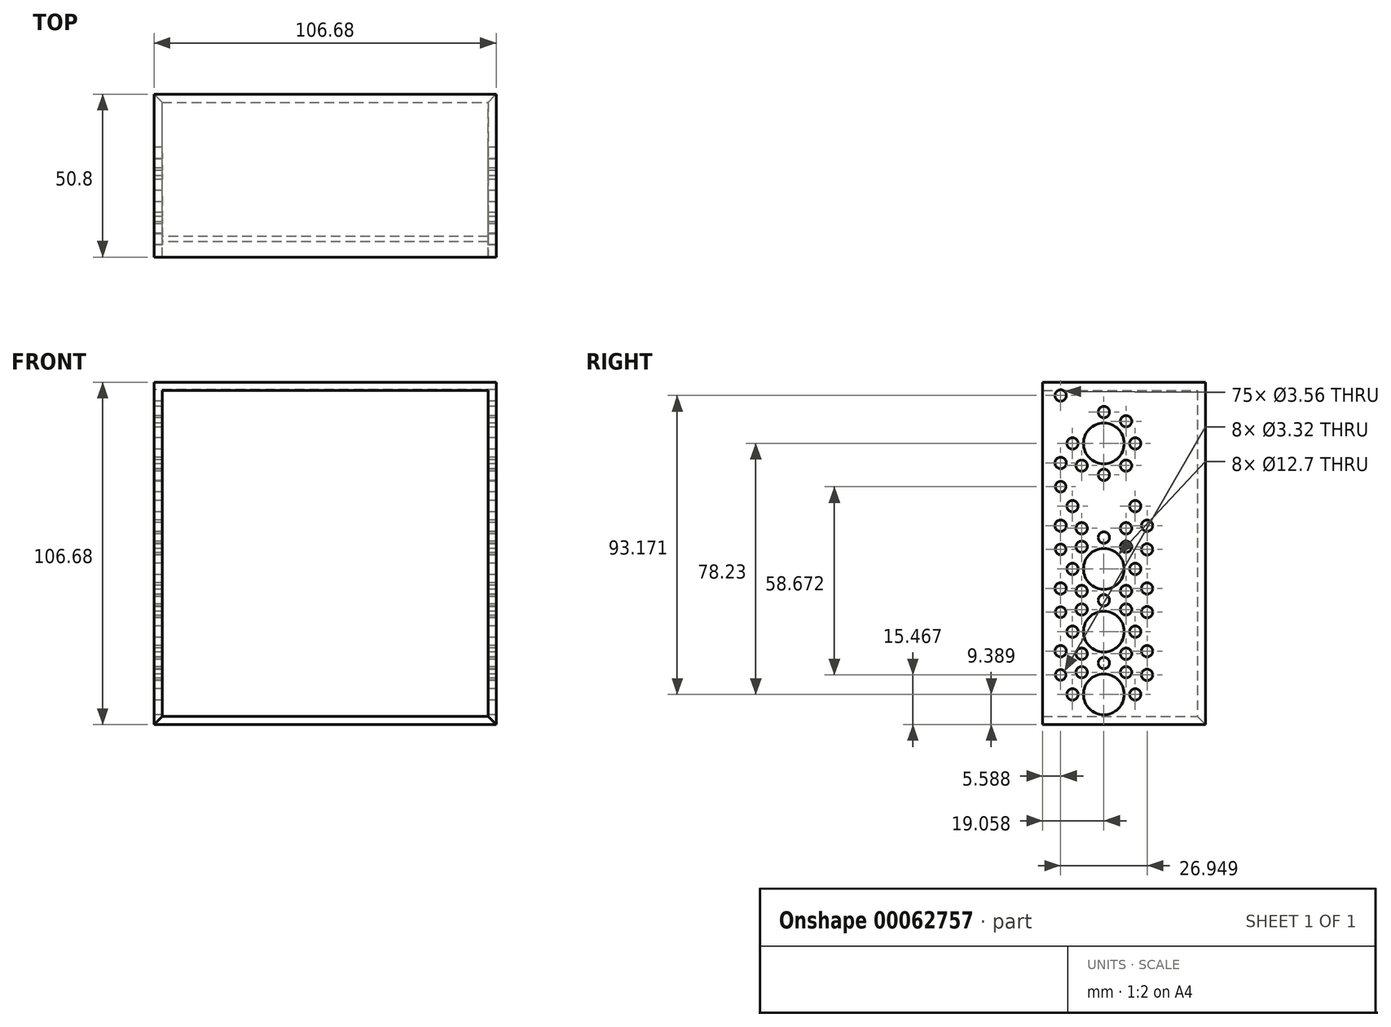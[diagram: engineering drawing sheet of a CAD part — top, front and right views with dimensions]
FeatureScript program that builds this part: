
annotation { "Feature Type Name" : "Feature", "Feature Type Description" : "" }
export const myFeature = defineFeature(function(context is Context, id is Id, definition is map)
    precondition{}
    {
        {
            var Q0;
            Q0=qCreatedBy(makeId("Front.planeOp"),FACE);
            var sketch = newSketch(context, id + "F0", { "sketchPlane" : qUnion([Q0])});
            skLineSegment(sketch, "E0.bottom", {"start": v(-57.75, 57.38) * mm, "end": v(48.93, 57.38) * mm});
            skLineSegment(sketch, "E0.top", {"start": v(-57.75, -49.3) * mm, "end": v(48.93, -49.3) * mm});
            skLineSegment(sketch, "E0.left", {"start": v(-57.75, 57.38) * mm, "end": v(-57.75, -49.3) * mm});
            skLineSegment(sketch, "E0.right", {"start": v(48.93, 57.38) * mm, "end": v(48.93, -49.3) * mm});
            skSolve(sketch);
        }
        {
            var Q0;
            Q0=makeQuery(id+"F0.imprint","IMPRINT",FACE,{"disambiguationData":[TD([[makeQuery(id+"F0.imprint","IMPRINT",EDGE,{"derivedFrom":sQuery(id+"F0.wireOp",EDGE,"E0.bottom")}),-1.0]])]});
            extrude(context, id + "F1", {"entities" : qUnion([Q0]), "depth" : 50.8 * mm});
        }
        {
            var Q0;
            Q0=makeQuery(id+"F1.opExtrude","CAP_FACE",FACE,{"disambiguationData":[OSD([sQuery(id+"F0.wireOp",EDGE,"E0.bottom"),sQuery(id+"F0.wireOp",EDGE,"E0.top"),sQuery(id+"F0.wireOp",EDGE,"E0.left"),sQuery(id+"F0.wireOp",EDGE,"E0.right")])],"isStart":false});
            var Q1;
            Q1=makeQuery(id+"F1.opExtrude","SWEPT_FACE",FACE,{"disambiguationData":[OSD([sQuery(id+"F0.wireOp",EDGE,"E0.top")])]});
            shell(context, id + "F2", {"entities" : qUnion([Q0, Q1]), "thickness" : 2.54 * mm});
        }
        {
            var Q0;
            {var subQ0=sQuery(id+"F0.wireOp",EDGE,"E0.top");Q0=makeQuery(id+"F2.opShell","OFFSET_EDGE",EDGE,{"disambiguationData":[OSD([subQ0]),TDD([makeQuery(id+"F1.opExtrude","CAP_EDGE",EDGE,{"disambiguationData":[OSD([subQ0])],"isStart":true})])]});}
            chamfer(context, id + "F3", {"entities" : qUnion([Q0]), "width" : 2.54 * mm, "tangentPropagation" : true});
        }
        {
            var Q0;
            Q0=makeQuery(id+"F2.opShell","OFFSET_EDGE",EDGE,{"disambiguationData":[OSD([sQuery(id+"F0.wireOp",EDGE,"E0.top"),sQuery(id+"F0.wireOp",EDGE,"E0.left")])]});
            chamfer(context, id + "F4", {"entities" : qUnion([Q0]), "width" : 2.54 * mm, "tangentPropagation" : true});
        }
        {
            var Q0;
            Q0=makeQuery(id+"F2.opShell","OFFSET_EDGE",EDGE,{"disambiguationData":[OSD([sQuery(id+"F0.wireOp",EDGE,"E0.top"),sQuery(id+"F0.wireOp",EDGE,"E0.right")])]});
            chamfer(context, id + "F5", {"entities" : qUnion([Q0]), "width" : 2.54 * mm, "tangentPropagation" : true});
        }
        {
            var Q0;
            Q0=makeQuery(id+"F1.opExtrude","SWEPT_FACE",FACE,{"disambiguationData":[OSD([sQuery(id+"F0.wireOp",EDGE,"E0.left")])]});
            var sketch = newSketch(context, id + "F6", { "sketchPlane" : qUnion([Q0])});
            skCircle(sketch, "E1", {"center": v(45.21, 53.26) * mm, "radius": 1.78 * mm});
            skCircle(sketch, "E2", {"center": v(18.26, 24.84) * mm, "radius": 1.78 * mm});
            skCircle(sketch, "E3", {"center": v(45.21, 24.84) * mm, "radius": 1.66 * mm});
            skCircle(sketch, "E4", {"center": v(38.66, 45.23) * mm, "radius": 1.78 * mm});
            skCircle(sketch, "E5", {"center": v(24.83, 31.4) * mm, "radius": 1.78 * mm});
            skCircle(sketch, "E6", {"center": v(31.74, 38.32) * mm, "radius": 6.35 * mm});
            skCircle(sketch, "E7", {"center": v(38.66, 31.4) * mm, "radius": 1.78 * mm});
            skCircle(sketch, "E8", {"center": v(24.83, 45.23) * mm, "radius": 1.78 * mm});
            skCircle(sketch, "E9", {"center": v(31.74, 48.1) * mm, "radius": 1.78 * mm});
            skCircle(sketch, "E10", {"center": v(21.96, 38.32) * mm, "radius": 1.78 * mm});
            skCircle(sketch, "E11", {"center": v(41.52, 38.32) * mm, "radius": 1.78 * mm});
            skCircle(sketch, "E12", {"center": v(31.74, 28.54) * mm, "radius": 1.78 * mm});
            skCircle(sketch, "E13.0.1.0", {"center": v(31.74, 8.98) * mm, "radius": 1.78 * mm});
            skCircle(sketch, "E13.0.1.1", {"center": v(31.74, 18.76) * mm, "radius": 6.35 * mm});
            skCircle(sketch, "E13.0.1.2", {"center": v(38.66, 11.85) * mm, "radius": 1.78 * mm});
            skCircle(sketch, "E13.0.1.3", {"center": v(41.52, 18.76) * mm, "radius": 1.78 * mm});
            skCircle(sketch, "E13.0.1.4", {"center": v(38.66, 25.68) * mm, "radius": 1.78 * mm});
            skCircle(sketch, "E13.0.1.5", {"center": v(45.21, 32.23) * mm, "radius": 1.78 * mm});
            skCircle(sketch, "E13.0.1.6", {"center": v(45.21, 5.28) * mm, "radius": 1.66 * mm});
            skCircle(sketch, "E13.0.1.7", {"center": v(24.83, 11.85) * mm, "radius": 1.78 * mm});
            skCircle(sketch, "E13.0.1.8", {"center": v(18.26, 5.28) * mm, "radius": 1.78 * mm});
            skCircle(sketch, "E13.0.1.9", {"center": v(21.96, 18.76) * mm, "radius": 1.78 * mm});
            skCircle(sketch, "E13.0.1.10", {"center": v(24.83, 25.68) * mm, "radius": 1.78 * mm});
            skCircle(sketch, "E13.0.1.12", {"center": v(18.26, 32.23) * mm, "radius": 1.78 * mm});
            skCircle(sketch, "E13.0.2.0", {"center": v(31.74, -10.58) * mm, "radius": 1.78 * mm});
            skCircle(sketch, "E13.0.2.1", {"center": v(31.74, -0.8) * mm, "radius": 6.35 * mm});
            skCircle(sketch, "E13.0.2.2", {"center": v(38.66, -7.71) * mm, "radius": 1.78 * mm});
            skCircle(sketch, "E13.0.2.3", {"center": v(41.52, -0.8) * mm, "radius": 1.78 * mm});
            skCircle(sketch, "E13.0.2.4", {"center": v(38.66, 6.12) * mm, "radius": 1.78 * mm});
            skCircle(sketch, "E13.0.2.5", {"center": v(45.21, 12.67) * mm, "radius": 1.78 * mm});
            skCircle(sketch, "E13.0.2.6", {"center": v(45.21, -14.28) * mm, "radius": 1.66 * mm});
            skCircle(sketch, "E13.0.2.7", {"center": v(24.83, -7.71) * mm, "radius": 1.78 * mm});
            skCircle(sketch, "E13.0.2.8", {"center": v(18.26, -14.28) * mm, "radius": 1.78 * mm});
            skCircle(sketch, "E13.0.2.9", {"center": v(21.96, -0.8) * mm, "radius": 1.78 * mm});
            skCircle(sketch, "E13.0.2.10", {"center": v(24.83, 6.12) * mm, "radius": 1.78 * mm});
            skCircle(sketch, "E13.0.2.11", {"center": v(31.74, 8.98) * mm, "radius": 1.78 * mm});
            skCircle(sketch, "E13.0.2.12", {"center": v(18.26, 12.67) * mm, "radius": 1.78 * mm});
            skCircle(sketch, "E13.0.3.0", {"center": v(31.74, -30.13) * mm, "radius": 1.78 * mm});
            skCircle(sketch, "E13.0.3.1", {"center": v(31.74, -20.35) * mm, "radius": 6.35 * mm});
            skCircle(sketch, "E13.0.3.2", {"center": v(38.66, -27.27) * mm, "radius": 1.78 * mm});
            skCircle(sketch, "E13.0.3.3", {"center": v(41.52, -20.35) * mm, "radius": 1.78 * mm});
            skCircle(sketch, "E13.0.3.4", {"center": v(38.66, -13.44) * mm, "radius": 1.78 * mm});
            skCircle(sketch, "E13.0.3.5", {"center": v(45.21, -6.88) * mm, "radius": 1.78 * mm});
            skCircle(sketch, "E13.0.3.6", {"center": v(45.21, -33.83) * mm, "radius": 1.66 * mm});
            skCircle(sketch, "E13.0.3.7", {"center": v(24.83, -27.27) * mm, "radius": 1.78 * mm});
            skCircle(sketch, "E13.0.3.8", {"center": v(18.26, -33.83) * mm, "radius": 1.78 * mm});
            skCircle(sketch, "E13.0.3.9", {"center": v(21.96, -20.35) * mm, "radius": 1.78 * mm});
            skCircle(sketch, "E13.0.3.10", {"center": v(24.83, -13.44) * mm, "radius": 1.78 * mm});
            skCircle(sketch, "E13.0.3.11", {"center": v(31.74, -10.57) * mm, "radius": 1.78 * mm});
            skCircle(sketch, "E13.0.3.12", {"center": v(18.26, -6.88) * mm, "radius": 1.78 * mm});
            skCircle(sketch, "E13.0.4.1", {"center": v(31.74, -39.91) * mm, "radius": 6.35 * mm});
            skCircle(sketch, "E13.0.4.3", {"center": v(41.52, -39.91) * mm, "radius": 1.78 * mm});
            skCircle(sketch, "E13.0.4.4", {"center": v(38.66, -33) * mm, "radius": 1.78 * mm});
            skCircle(sketch, "E13.0.4.5", {"center": v(45.21, -26.44) * mm, "radius": 1.78 * mm});
            skCircle(sketch, "E13.0.4.9", {"center": v(21.96, -39.91) * mm, "radius": 1.78 * mm});
            skCircle(sketch, "E13.0.4.10", {"center": v(24.83, -33) * mm, "radius": 1.78 * mm});
            skCircle(sketch, "E13.0.4.11", {"center": v(31.74, -30.13) * mm, "radius": 1.78 * mm});
            skCircle(sketch, "E13.0.4.12", {"center": v(18.26, -26.44) * mm, "radius": 1.78 * mm});
            skLineSegment(sketch, "E13.direction2", {"start": v(31.74, 28.54) * mm, "end": v(31.74, 8.98) * mm, "construction": true});
            skCircle(sketch, "E14", {"center": v(24.83, 49.96) * mm, "radius": 1.78 * mm});
            skCircle(sketch, "E15", {"center": v(38.66, 49.96) * mm, "radius": 1.78 * mm});
            skCircle(sketch, "E16", {"center": v(45.21, 45.36) * mm, "radius": 1.78 * mm});
            skCircle(sketch, "E17", {"center": v(18.26, 53.31) * mm, "radius": 1.78 * mm});
            skCircle(sketch, "E18", {"center": v(18.26, 45.25) * mm, "radius": 1.78 * mm});
            skSolve(sketch);
        }
        {
            var Q0;
            Q0=makeQuery(id+"F6.imprint","IMPRINT",FACE,{"disambiguationData":[TD([[makeQuery(id+"F6.imprint","IMPRINT",EDGE,{"derivedFrom":sQuery(id+"F6.wireOp",EDGE,"E3")}),1.0]])]});
            var Q1;
            Q1=makeQuery(id+"F6.imprint","IMPRINT",FACE,{"disambiguationData":[TD([[makeQuery(id+"F6.imprint","IMPRINT",EDGE,{"derivedFrom":sQuery(id+"F6.wireOp",EDGE,"E5")}),1.0]])]});
            var Q2;
            Q2=makeQuery(id+"F6.imprint","IMPRINT",FACE,{"disambiguationData":[TD([[makeQuery(id+"F6.imprint","IMPRINT",EDGE,{"derivedFrom":sQuery(id+"F6.wireOp",EDGE,"E7")}),1.0]])]});
            var Q3;
            Q3=makeQuery(id+"F6.imprint","IMPRINT",FACE,{"disambiguationData":[TD([[makeQuery(id+"F6.imprint","IMPRINT",EDGE,{"derivedFrom":sQuery(id+"F6.wireOp",EDGE,"E8")}),1.0]])]});
            var Q4;
            Q4=makeQuery(id+"F6.imprint","IMPRINT",FACE,{"disambiguationData":[TD([[makeQuery(id+"F6.imprint","IMPRINT",EDGE,{"derivedFrom":sQuery(id+"F6.wireOp",EDGE,"E9")}),1.0]])]});
            var Q5;
            Q5=makeQuery(id+"F6.imprint","IMPRINT",FACE,{"disambiguationData":[TD([[makeQuery(id+"F6.imprint","IMPRINT",EDGE,{"derivedFrom":sQuery(id+"F6.wireOp",EDGE,"E10")}),1.0]])]});
            var Q6;
            Q6=makeQuery(id+"F6.imprint","IMPRINT",FACE,{"disambiguationData":[TD([[makeQuery(id+"F6.imprint","IMPRINT",EDGE,{"derivedFrom":sQuery(id+"F6.wireOp",EDGE,"E11")}),1.0]])]});
            var Q7;
            Q7=makeQuery(id+"F6.imprint","IMPRINT",FACE,{"disambiguationData":[TD([[makeQuery(id+"F6.imprint","IMPRINT",EDGE,{"derivedFrom":sQuery(id+"F6.wireOp",EDGE,"E13.0.1.2")}),1.0]])]});
            var Q8;
            Q8=makeQuery(id+"F6.imprint","IMPRINT",FACE,{"disambiguationData":[TD([[makeQuery(id+"F6.imprint","IMPRINT",EDGE,{"derivedFrom":sQuery(id+"F6.wireOp",EDGE,"E13.0.1.3")}),1.0]])]});
            var Q9;
            Q9=makeQuery(id+"F6.imprint","IMPRINT",FACE,{"disambiguationData":[TD([[makeQuery(id+"F6.imprint","IMPRINT",EDGE,{"derivedFrom":sQuery(id+"F6.wireOp",EDGE,"E13.0.1.5")}),1.0]])]});
            var Q10;
            Q10=makeQuery(id+"F6.imprint","IMPRINT",FACE,{"disambiguationData":[TD([[makeQuery(id+"F6.imprint","IMPRINT",EDGE,{"derivedFrom":sQuery(id+"F6.wireOp",EDGE,"E13.0.1.6")}),1.0]])]});
            var Q11;
            Q11=makeQuery(id+"F6.imprint","IMPRINT",FACE,{"disambiguationData":[TD([[makeQuery(id+"F6.imprint","IMPRINT",EDGE,{"derivedFrom":sQuery(id+"F6.wireOp",EDGE,"E13.0.1.7")}),1.0]])]});
            var Q12;
            Q12=makeQuery(id+"F6.imprint","IMPRINT",FACE,{"disambiguationData":[TD([[makeQuery(id+"F6.imprint","IMPRINT",EDGE,{"derivedFrom":sQuery(id+"F6.wireOp",EDGE,"E13.0.1.8")}),1.0]])]});
            var Q13;
            Q13=makeQuery(id+"F6.imprint","IMPRINT",FACE,{"disambiguationData":[TD([[makeQuery(id+"F6.imprint","IMPRINT",EDGE,{"derivedFrom":sQuery(id+"F6.wireOp",EDGE,"E13.0.1.9")}),1.0]])]});
            var Q14;
            Q14=makeQuery(id+"F6.imprint","IMPRINT",FACE,{"disambiguationData":[TD([[makeQuery(id+"F6.imprint","IMPRINT",EDGE,{"derivedFrom":sQuery(id+"F6.wireOp",EDGE,"E13.0.2.1")}),1.0]])]});
            var Q15;
            Q15=makeQuery(id+"F6.imprint","IMPRINT",FACE,{"disambiguationData":[TD([[makeQuery(id+"F6.imprint","IMPRINT",EDGE,{"derivedFrom":sQuery(id+"F6.wireOp",EDGE,"E13.0.2.2")}),1.0]])]});
            var Q16;
            Q16=makeQuery(id+"F6.imprint","IMPRINT",FACE,{"disambiguationData":[TD([[makeQuery(id+"F6.imprint","IMPRINT",EDGE,{"derivedFrom":sQuery(id+"F6.wireOp",EDGE,"E13.0.2.3")}),1.0]])]});
            var Q17;
            Q17=makeQuery(id+"F6.imprint","IMPRINT",FACE,{"disambiguationData":[TD([[makeQuery(id+"F6.imprint","IMPRINT",EDGE,{"derivedFrom":sQuery(id+"F6.wireOp",EDGE,"E13.0.2.4")}),1.0]])]});
            var Q18;
            Q18=makeQuery(id+"F6.imprint","IMPRINT",FACE,{"disambiguationData":[TD([[makeQuery(id+"F6.imprint","IMPRINT",EDGE,{"derivedFrom":sQuery(id+"F6.wireOp",EDGE,"E13.0.2.5")}),1.0]])]});
            var Q19;
            Q19=makeQuery(id+"F6.imprint","IMPRINT",FACE,{"disambiguationData":[TD([[makeQuery(id+"F6.imprint","IMPRINT",EDGE,{"derivedFrom":sQuery(id+"F6.wireOp",EDGE,"E13.0.2.6")}),1.0]])]});
            var Q20;
            Q20=makeQuery(id+"F6.imprint","IMPRINT",FACE,{"disambiguationData":[TD([[makeQuery(id+"F6.imprint","IMPRINT",EDGE,{"derivedFrom":sQuery(id+"F6.wireOp",EDGE,"E13.0.2.7")}),1.0]])]});
            var Q21;
            Q21=makeQuery(id+"F6.imprint","IMPRINT",FACE,{"disambiguationData":[TD([[makeQuery(id+"F6.imprint","IMPRINT",EDGE,{"derivedFrom":sQuery(id+"F6.wireOp",EDGE,"E13.0.2.8")}),1.0]])]});
            var Q22;
            Q22=makeQuery(id+"F6.imprint","IMPRINT",FACE,{"disambiguationData":[TD([[makeQuery(id+"F6.imprint","IMPRINT",EDGE,{"derivedFrom":sQuery(id+"F6.wireOp",EDGE,"E13.0.2.9")}),1.0]])]});
            var Q23;
            Q23=makeQuery(id+"F6.imprint","IMPRINT",FACE,{"disambiguationData":[TD([[makeQuery(id+"F6.imprint","IMPRINT",EDGE,{"derivedFrom":sQuery(id+"F6.wireOp",EDGE,"E13.0.2.10")}),1.0]])]});
            var Q24;
            Q24=makeQuery(id+"F6.imprint","IMPRINT",FACE,{"disambiguationData":[TD([[makeQuery(id+"F6.imprint","IMPRINT",EDGE,{"derivedFrom":sQuery(id+"F6.wireOp",EDGE,"E13.0.2.12")}),1.0]])]});
            var Q25;
            Q25=makeQuery(id+"F6.imprint","IMPRINT",FACE,{"disambiguationData":[TD([[makeQuery(id+"F6.imprint","IMPRINT",EDGE,{"derivedFrom":sQuery(id+"F6.wireOp",EDGE,"E13.0.3.1")}),1.0]])]});
            var Q26;
            Q26=makeQuery(id+"F6.imprint","IMPRINT",FACE,{"disambiguationData":[TD([[makeQuery(id+"F6.imprint","IMPRINT",EDGE,{"derivedFrom":sQuery(id+"F6.wireOp",EDGE,"E13.0.3.2")}),1.0]])]});
            var Q27;
            Q27=makeQuery(id+"F6.imprint","IMPRINT",FACE,{"disambiguationData":[TD([[makeQuery(id+"F6.imprint","IMPRINT",EDGE,{"derivedFrom":sQuery(id+"F6.wireOp",EDGE,"E13.0.3.3")}),1.0]])]});
            var Q28;
            Q28=makeQuery(id+"F6.imprint","IMPRINT",FACE,{"disambiguationData":[TD([[makeQuery(id+"F6.imprint","IMPRINT",EDGE,{"derivedFrom":sQuery(id+"F6.wireOp",EDGE,"E13.0.3.4")}),1.0]])]});
            var Q29;
            Q29=makeQuery(id+"F6.imprint","IMPRINT",FACE,{"disambiguationData":[TD([[makeQuery(id+"F6.imprint","IMPRINT",EDGE,{"derivedFrom":sQuery(id+"F6.wireOp",EDGE,"E13.0.3.5")}),1.0]])]});
            var Q30;
            Q30=makeQuery(id+"F6.imprint","IMPRINT",FACE,{"disambiguationData":[TD([[makeQuery(id+"F6.imprint","IMPRINT",EDGE,{"derivedFrom":sQuery(id+"F6.wireOp",EDGE,"E13.0.3.6")}),1.0]])]});
            var Q31;
            Q31=makeQuery(id+"F6.imprint","IMPRINT",FACE,{"disambiguationData":[TD([[makeQuery(id+"F6.imprint","IMPRINT",EDGE,{"derivedFrom":sQuery(id+"F6.wireOp",EDGE,"E13.0.3.7")}),1.0]])]});
            var Q32;
            Q32=makeQuery(id+"F6.imprint","IMPRINT",FACE,{"disambiguationData":[TD([[makeQuery(id+"F6.imprint","IMPRINT",EDGE,{"derivedFrom":sQuery(id+"F6.wireOp",EDGE,"E13.0.3.8")}),1.0]])]});
            var Q33;
            Q33=makeQuery(id+"F6.imprint","IMPRINT",FACE,{"disambiguationData":[TD([[makeQuery(id+"F6.imprint","IMPRINT",EDGE,{"derivedFrom":sQuery(id+"F6.wireOp",EDGE,"E13.0.3.9")}),1.0]])]});
            var Q34;
            Q34=makeQuery(id+"F6.imprint","IMPRINT",FACE,{"disambiguationData":[TD([[makeQuery(id+"F6.imprint","IMPRINT",EDGE,{"derivedFrom":sQuery(id+"F6.wireOp",EDGE,"E13.0.3.10")}),1.0]])]});
            var Q35;
            Q35=makeQuery(id+"F6.imprint","IMPRINT",FACE,{"disambiguationData":[TD([[makeQuery(id+"F6.imprint","IMPRINT",EDGE,{"derivedFrom":sQuery(id+"F6.wireOp",EDGE,"E13.0.3.12")}),1.0]])]});
            var Q36;
            Q36=makeQuery(id+"F6.imprint","IMPRINT",FACE,{"disambiguationData":[TD([[makeQuery(id+"F6.imprint","IMPRINT",EDGE,{"derivedFrom":sQuery(id+"F6.wireOp",EDGE,"E13.0.4.1")}),1.0]])]});
            var Q37;
            Q37=makeQuery(id+"F6.imprint","IMPRINT",FACE,{"disambiguationData":[TD([[makeQuery(id+"F6.imprint","IMPRINT",EDGE,{"derivedFrom":sQuery(id+"F6.wireOp",EDGE,"E13.0.4.3")}),1.0]])]});
            var Q38;
            Q38=makeQuery(id+"F6.imprint","IMPRINT",FACE,{"disambiguationData":[TD([[makeQuery(id+"F6.imprint","IMPRINT",EDGE,{"derivedFrom":sQuery(id+"F6.wireOp",EDGE,"E13.0.4.4")}),1.0]])]});
            var Q39;
            Q39=makeQuery(id+"F6.imprint","IMPRINT",FACE,{"disambiguationData":[TD([[makeQuery(id+"F6.imprint","IMPRINT",EDGE,{"derivedFrom":sQuery(id+"F6.wireOp",EDGE,"E13.0.4.5")}),1.0]])]});
            var Q40;
            Q40=makeQuery(id+"F6.imprint","IMPRINT",FACE,{"disambiguationData":[TD([[makeQuery(id+"F6.imprint","IMPRINT",EDGE,{"derivedFrom":sQuery(id+"F6.wireOp",EDGE,"E13.0.4.9")}),1.0]])]});
            var Q41;
            Q41=makeQuery(id+"F6.imprint","IMPRINT",FACE,{"disambiguationData":[TD([[makeQuery(id+"F6.imprint","IMPRINT",EDGE,{"derivedFrom":sQuery(id+"F6.wireOp",EDGE,"E13.0.4.10")}),1.0]])]});
            var Q42;
            Q42=makeQuery(id+"F6.imprint","IMPRINT",FACE,{"disambiguationData":[TD([[makeQuery(id+"F6.imprint","IMPRINT",EDGE,{"derivedFrom":sQuery(id+"F6.wireOp",EDGE,"E13.0.4.12")}),1.0]])]});
            var Q43;
            {var subQ0=sQuery(id+"F6.wireOp",EDGE,"A2h9f5pg-UWyG-NB71-LqB8-NmD9h6sl18N1");var subQ1=sQuery(id+"F6.wireOp",EDGE,"vdxriytp-X9rP-He6E-1Lm6-v2A8iyULkwqD");var subQ2=makeQuery(id+"F6.imprint","INTERSECT",VERTEX,{"derivedFrom":[subQ1,subQ0]});Q43=makeQuery(id+"F6.imprint","IMPRINT",FACE,{"disambiguationData":[TD([[makeQuery(id+"F6.imprint","IMPRINT",EDGE,{"disambiguationData":[TD([[subQ2,1.0]])],"derivedFrom":subQ1}),-1.0]])]});}
            var Q44;
            {var subQ0=sQuery(id+"F6.wireOp",EDGE,"A2h9f5pg-UWyG-NB71-LqB8-NmD9h6sl18N1");var subQ1=sQuery(id+"F6.wireOp",EDGE,"vdxriytp-X9rP-He6E-1Lm6-v2A8iyULkwqD");var subQ2=makeQuery(id+"F6.imprint","INTERSECT",VERTEX,{"derivedFrom":[subQ1,subQ0]});Q44=makeQuery(id+"F6.imprint","IMPRINT",FACE,{"disambiguationData":[TD([[makeQuery(id+"F6.imprint","IMPRINT",EDGE,{"disambiguationData":[TD([[subQ2,1.0]])],"derivedFrom":subQ1}),1.0]])]});}
            var Q45;
            {var subQ0=sQuery(id+"F6.wireOp",EDGE,"E13.0.1.12");var subQ1=sQuery(id+"F6.wireOp",EDGE,"A2h9f5pg-UWyG-NB71-LqB8-NmD9h6sl18N1");var subQ2=makeQuery(id+"F6.imprint","INTERSECT",VERTEX,{"disambiguationData":[OD(0.0)],"derivedFrom":[subQ1,subQ0]});Q45=makeQuery(id+"F6.imprint","IMPRINT",FACE,{"disambiguationData":[TD([[makeQuery(id+"F6.imprint","IMPRINT",EDGE,{"disambiguationData":[TD([[subQ2,1.0]])],"derivedFrom":subQ1}),-1.0]])]});}
            var Q46;
            {var subQ0=sQuery(id+"F6.wireOp",EDGE,"E13.0.1.12");var subQ1=sQuery(id+"F6.wireOp",EDGE,"A2h9f5pg-UWyG-NB71-LqB8-NmD9h6sl18N1");var subQ2=makeQuery(id+"F6.imprint","INTERSECT",VERTEX,{"disambiguationData":[OD(0.0)],"derivedFrom":[subQ1,subQ0]});Q46=makeQuery(id+"F6.imprint","IMPRINT",FACE,{"disambiguationData":[TD([[makeQuery(id+"F6.imprint","IMPRINT",EDGE,{"disambiguationData":[TD([[subQ2,1.0]])],"derivedFrom":subQ1}),1.0]])]});}
            var Q47;
            {var subQ0=sQuery(id+"F6.wireOp",EDGE,"owMZy3Z5-PBnJ-gcCq-pzpr-cYzJ99XcFTPD");var subQ1=sQuery(id+"F6.wireOp",EDGE,"A2h9f5pg-UWyG-NB71-LqB8-NmD9h6sl18N1");var subQ2=makeQuery(id+"F6.imprint","INTERSECT",VERTEX,{"derivedFrom":[subQ1,subQ0]});Q47=makeQuery(id+"F6.imprint","IMPRINT",FACE,{"disambiguationData":[TD([[makeQuery(id+"F6.imprint","IMPRINT",EDGE,{"disambiguationData":[TD([[subQ2,1.0]])],"derivedFrom":subQ1}),1.0]])]});}
            var Q48;
            {var subQ0=sQuery(id+"F6.wireOp",EDGE,"owMZy3Z5-PBnJ-gcCq-pzpr-cYzJ99XcFTPD");var subQ1=sQuery(id+"F6.wireOp",EDGE,"A2h9f5pg-UWyG-NB71-LqB8-NmD9h6sl18N1");var subQ2=makeQuery(id+"F6.imprint","INTERSECT",VERTEX,{"derivedFrom":[subQ1,subQ0]});Q48=makeQuery(id+"F6.imprint","IMPRINT",FACE,{"disambiguationData":[TD([[makeQuery(id+"F6.imprint","IMPRINT",EDGE,{"disambiguationData":[TD([[subQ2,1.0]])],"derivedFrom":subQ1}),-1.0]])]});}
            var Q49;
            {var subQ0=sQuery(id+"F6.wireOp",EDGE,"E13.0.1.10");var subQ1=sQuery(id+"F6.wireOp",EDGE,"owMZy3Z5-PBnJ-gcCq-pzpr-cYzJ99XcFTPD");var subQ2=makeQuery(id+"F6.imprint","INTERSECT",VERTEX,{"disambiguationData":[OD(0.0)],"derivedFrom":[subQ1,subQ0]});Q49=makeQuery(id+"F6.imprint","IMPRINT",FACE,{"disambiguationData":[TD([[makeQuery(id+"F6.imprint","IMPRINT",EDGE,{"disambiguationData":[TD([[subQ2,1.0]])],"derivedFrom":subQ1}),-1.0]])]});}
            var Q50;
            {var subQ0=sQuery(id+"F6.wireOp",EDGE,"E13.0.1.10");var subQ1=sQuery(id+"F6.wireOp",EDGE,"owMZy3Z5-PBnJ-gcCq-pzpr-cYzJ99XcFTPD");var subQ2=makeQuery(id+"F6.imprint","INTERSECT",VERTEX,{"disambiguationData":[OD(0.0)],"derivedFrom":[subQ1,subQ0]});Q50=makeQuery(id+"F6.imprint","IMPRINT",FACE,{"disambiguationData":[TD([[makeQuery(id+"F6.imprint","IMPRINT",EDGE,{"disambiguationData":[TD([[subQ2,1.0]])],"derivedFrom":subQ1}),1.0]])]});}
            var Q51;
            {var subQ0=sQuery(id+"F6.wireOp",EDGE,"E13.0.1.1");var subQ1=sQuery(id+"F6.wireOp",EDGE,"owMZy3Z5-PBnJ-gcCq-pzpr-cYzJ99XcFTPD");var subQ2=makeQuery(id+"F6.imprint","INTERSECT",VERTEX,{"disambiguationData":[OD(0.0)],"derivedFrom":[subQ1,subQ0]});Q51=makeQuery(id+"F6.imprint","IMPRINT",FACE,{"disambiguationData":[TD([[makeQuery(id+"F6.imprint","IMPRINT",EDGE,{"disambiguationData":[TD([[subQ2,1.0]])],"derivedFrom":subQ1}),1.0]])]});}
            var Q52;
            {var subQ0=sQuery(id+"F6.wireOp",EDGE,"E13.0.1.1");var subQ1=sQuery(id+"F6.wireOp",EDGE,"owMZy3Z5-PBnJ-gcCq-pzpr-cYzJ99XcFTPD");var subQ2=makeQuery(id+"F6.imprint","INTERSECT",VERTEX,{"disambiguationData":[OD(0.0)],"derivedFrom":[subQ1,subQ0]});Q52=makeQuery(id+"F6.imprint","IMPRINT",FACE,{"disambiguationData":[TD([[makeQuery(id+"F6.imprint","IMPRINT",EDGE,{"disambiguationData":[TD([[subQ2,1.0]])],"derivedFrom":subQ1}),-1.0]])]});}
            var Q53;
            {var subQ0=sQuery(id+"F6.wireOp",EDGE,"E13.0.1.4");var subQ1=sQuery(id+"F6.wireOp",EDGE,"owMZy3Z5-PBnJ-gcCq-pzpr-cYzJ99XcFTPD");var subQ2=makeQuery(id+"F6.imprint","INTERSECT",VERTEX,{"disambiguationData":[OD(0.0)],"derivedFrom":[subQ1,subQ0]});Q53=makeQuery(id+"F6.imprint","IMPRINT",FACE,{"disambiguationData":[TD([[makeQuery(id+"F6.imprint","IMPRINT",EDGE,{"disambiguationData":[TD([[subQ2,1.0]])],"derivedFrom":subQ1}),-1.0]])]});}
            var Q54;
            {var subQ0=sQuery(id+"F6.wireOp",EDGE,"E13.0.1.4");var subQ1=sQuery(id+"F6.wireOp",EDGE,"owMZy3Z5-PBnJ-gcCq-pzpr-cYzJ99XcFTPD");var subQ2=makeQuery(id+"F6.imprint","INTERSECT",VERTEX,{"disambiguationData":[OD(0.0)],"derivedFrom":[subQ1,subQ0]});Q54=makeQuery(id+"F6.imprint","IMPRINT",FACE,{"disambiguationData":[TD([[makeQuery(id+"F6.imprint","IMPRINT",EDGE,{"disambiguationData":[TD([[subQ2,1.0]])],"derivedFrom":subQ1}),1.0]])]});}
            var Q55;
            {var subQ0=sQuery(id+"F6.wireOp",EDGE,"KO0H5Guw-bcFE-xj2E-t414-NG06jMZt0GET");var subQ1=sQuery(id+"F6.wireOp",EDGE,"slbY2Bo9-q9ib-zJOt-UMSs-wo7bCMDzegcF");var subQ2=makeQuery(id+"F6.imprint","INTERSECT",VERTEX,{"derivedFrom":[subQ1,subQ0]});Q55=makeQuery(id+"F6.imprint","IMPRINT",FACE,{"disambiguationData":[TD([[makeQuery(id+"F6.imprint","IMPRINT",EDGE,{"disambiguationData":[TD([[subQ2,1.0]])],"derivedFrom":subQ1}),-1.0]])]});}
            var Q56;
            {var subQ0=sQuery(id+"F6.wireOp",EDGE,"KO0H5Guw-bcFE-xj2E-t414-NG06jMZt0GET");var subQ1=sQuery(id+"F6.wireOp",EDGE,"slbY2Bo9-q9ib-zJOt-UMSs-wo7bCMDzegcF");var subQ2=makeQuery(id+"F6.imprint","INTERSECT",VERTEX,{"derivedFrom":[subQ1,subQ0]});Q56=makeQuery(id+"F6.imprint","IMPRINT",FACE,{"disambiguationData":[TD([[makeQuery(id+"F6.imprint","IMPRINT",EDGE,{"disambiguationData":[TD([[subQ2,1.0]])],"derivedFrom":subQ1}),1.0]])]});}
            var Q57;
            {var subQ0=sQuery(id+"F6.wireOp",EDGE,"E13.0.2.11");var subQ1=sQuery(id+"F6.wireOp",EDGE,"E13.0.1.0");var subQ2=makeQuery(id+"F6.imprint","INTERSECT",VERTEX,{"disambiguationData":[OD(0.0)],"derivedFrom":[subQ1,subQ0]});Q57=makeQuery(id+"F6.imprint","IMPRINT",FACE,{"disambiguationData":[TD([[makeQuery(id+"F6.imprint","IMPRINT",EDGE,{"disambiguationData":[TD([[subQ2,-1.0]])],"derivedFrom":subQ1}),1.0]])]});}
            var Q58;
            {var subQ0=sQuery(id+"F6.wireOp",EDGE,"E13.0.3.11");var subQ1=sQuery(id+"F6.wireOp",EDGE,"E13.0.2.0");var subQ2=makeQuery(id+"F6.imprint","INTERSECT",VERTEX,{"disambiguationData":[OD(0.0)],"derivedFrom":[subQ1,subQ0]});Q58=makeQuery(id+"F6.imprint","IMPRINT",FACE,{"disambiguationData":[TD([[makeQuery(id+"F6.imprint","IMPRINT",EDGE,{"disambiguationData":[TD([[subQ2,-1.0]])],"derivedFrom":subQ1}),1.0]])]});}
            var Q59;
            {var subQ0=sQuery(id+"F6.wireOp",EDGE,"E13.0.4.11");var subQ1=sQuery(id+"F6.wireOp",EDGE,"E13.0.3.0");var subQ2=makeQuery(id+"F6.imprint","INTERSECT",VERTEX,{"disambiguationData":[OD(0.0)],"derivedFrom":[subQ1,subQ0]});Q59=makeQuery(id+"F6.imprint","IMPRINT",FACE,{"disambiguationData":[TD([[makeQuery(id+"F6.imprint","IMPRINT",EDGE,{"disambiguationData":[TD([[subQ2,-1.0]])],"derivedFrom":subQ1}),1.0]])]});}
            var Q60;
            {var subQ1=sQuery(id+"F6.wireOp",EDGE,"e0d9b2b3-a0e2-4803-aa03-cc39501d7701.top");var subQ3=sQuery(id+"F6.wireOp",EDGE,"E1");var subQ4=makeQuery(id+"F6.imprint","INTERSECT",VERTEX,{"derivedFrom":[subQ1,subQ3]});Q60=makeQuery(id+"F6.imprint","IMPRINT",FACE,{"disambiguationData":[TD([[makeQuery(id+"F6.imprint","IMPRINT",EDGE,{"disambiguationData":[TD([[subQ4,-1.0]])],"derivedFrom":subQ3}),1.0]])]});}
            var Q61;
            {var subQ0=sQuery(id+"F6.wireOp",EDGE,"slbY2Bo9-q9ib-zJOt-UMSs-wo7bCMDzegcF");var subQ3=sQuery(id+"F6.wireOp",EDGE,"E1");var subQ5=makeQuery(id+"F6.imprint","INTERSECT",VERTEX,{"derivedFrom":[subQ3,subQ0]});Q61=makeQuery(id+"F6.imprint","IMPRINT",FACE,{"disambiguationData":[TD([[makeQuery(id+"F6.imprint","IMPRINT",EDGE,{"disambiguationData":[TD([[subQ5,-1.0]])],"derivedFrom":subQ3}),1.0]])]});}
            var Q62;
            {var subQ0=sQuery(id+"F6.wireOp",EDGE,"vdxriytp-X9rP-He6E-1Lm6-v2A8iyULkwqD");var subQ3=sQuery(id+"F6.wireOp",EDGE,"E1");var subQ5=makeQuery(id+"F6.imprint","INTERSECT",VERTEX,{"derivedFrom":[subQ3,subQ0]});Q62=makeQuery(id+"F6.imprint","IMPRINT",FACE,{"disambiguationData":[TD([[makeQuery(id+"F6.imprint","IMPRINT",EDGE,{"disambiguationData":[TD([[subQ5,1.0]])],"derivedFrom":subQ3}),1.0]])]});}
            var Q63;
            {var subQ0=sQuery(id+"F6.wireOp",EDGE,"vdxriytp-X9rP-He6E-1Lm6-v2A8iyULkwqD");var subQ1=sQuery(id+"F6.wireOp",EDGE,"E1");var subQ2=makeQuery(id+"F6.imprint","INTERSECT",VERTEX,{"derivedFrom":[subQ1,subQ0]});Q63=makeQuery(id+"F6.imprint","IMPRINT",FACE,{"disambiguationData":[TD([[makeQuery(id+"F6.imprint","IMPRINT",EDGE,{"disambiguationData":[TD([[subQ2,-1.0]])],"derivedFrom":subQ1}),1.0]])]});}
            var Q64;
            {var subQ1=sQuery(id+"F6.wireOp",EDGE,"KO0H5Guw-bcFE-xj2E-t414-NG06jMZt0GET");var subQ3=sQuery(id+"F6.wireOp",EDGE,"E6");var subQ4=makeQuery(id+"F6.imprint","INTERSECT",VERTEX,{"derivedFrom":[subQ1,subQ3]});Q64=makeQuery(id+"F6.imprint","IMPRINT",FACE,{"disambiguationData":[TD([[makeQuery(id+"F6.imprint","IMPRINT",EDGE,{"disambiguationData":[TD([[subQ4,1.0]])],"derivedFrom":subQ3}),1.0]])]});}
            var Q65;
            {var subQ1=sQuery(id+"F6.wireOp",EDGE,"KO0H5Guw-bcFE-xj2E-t414-NG06jMZt0GET");var subQ3=sQuery(id+"F6.wireOp",EDGE,"E6");var subQ4=makeQuery(id+"F6.imprint","INTERSECT",VERTEX,{"derivedFrom":[subQ1,subQ3]});Q65=makeQuery(id+"F6.imprint","IMPRINT",FACE,{"disambiguationData":[TD([[makeQuery(id+"F6.imprint","IMPRINT",EDGE,{"disambiguationData":[TD([[subQ4,-1.0]])],"derivedFrom":subQ3}),1.0]])]});}
            var Q66;
            {var subQ0=sQuery(id+"F6.wireOp",EDGE,"CGZUbKsU-e6iw-QqdH-Tbkk-jQw2wMSzCloF");var subQ1=sQuery(id+"F6.wireOp",EDGE,"E6");var subQ2=makeQuery(id+"F6.imprint","INTERSECT",VERTEX,{"derivedFrom":[subQ1,subQ0]});Q66=makeQuery(id+"F6.imprint","IMPRINT",FACE,{"disambiguationData":[TD([[makeQuery(id+"F6.imprint","IMPRINT",EDGE,{"disambiguationData":[TD([[subQ2,-1.0]])],"derivedFrom":subQ1}),1.0]])]});}
            var Q67;
            {var subQ0=sQuery(id+"F6.wireOp",EDGE,"4vIWURT5-V69c-NRQ5-y8tq-tIsSe4MiV3SC");var subQ1=sQuery(id+"F6.wireOp",EDGE,"E6");var subQ2=makeQuery(id+"F6.imprint","INTERSECT",VERTEX,{"derivedFrom":[subQ1,subQ0]});Q67=makeQuery(id+"F6.imprint","IMPRINT",FACE,{"disambiguationData":[TD([[makeQuery(id+"F6.imprint","IMPRINT",EDGE,{"disambiguationData":[TD([[subQ2,-1.0]])],"derivedFrom":subQ1}),1.0]])]});}
            var Q68;
            {var subQ0=sQuery(id+"F6.wireOp",EDGE,"enhWjaKT-P2pr-CgfV-l5od-zM1snsL3nqsT");var subQ1=sQuery(id+"F6.wireOp",EDGE,"E6");var subQ2=makeQuery(id+"F6.imprint","INTERSECT",VERTEX,{"derivedFrom":[subQ1,subQ0]});Q68=makeQuery(id+"F6.imprint","IMPRINT",FACE,{"disambiguationData":[TD([[makeQuery(id+"F6.imprint","IMPRINT",EDGE,{"disambiguationData":[TD([[subQ2,1.0]])],"derivedFrom":subQ1}),1.0]])]});}
            var Q69;
            {var subQ0=sQuery(id+"F6.wireOp",EDGE,"E12");var subQ1=sQuery(id+"F6.wireOp",EDGE,"Tb1vFxD2-eZhD-3B21-jOu3-oEgeX6T2umbS");var subQ2=makeQuery(id+"F6.imprint","INTERSECT",VERTEX,{"derivedFrom":[subQ1,subQ0]});Q69=makeQuery(id+"F6.imprint","IMPRINT",FACE,{"disambiguationData":[TD([[makeQuery(id+"F6.imprint","IMPRINT",EDGE,{"disambiguationData":[TD([[subQ2,1.0]])],"derivedFrom":subQ1}),1.0]])]});}
            var Q70;
            {var subQ0=sQuery(id+"F6.wireOp",EDGE,"E12");var subQ1=sQuery(id+"F6.wireOp",EDGE,"Tb1vFxD2-eZhD-3B21-jOu3-oEgeX6T2umbS");var subQ2=makeQuery(id+"F6.imprint","INTERSECT",VERTEX,{"derivedFrom":[subQ1,subQ0]});Q70=makeQuery(id+"F6.imprint","IMPRINT",FACE,{"disambiguationData":[TD([[makeQuery(id+"F6.imprint","IMPRINT",EDGE,{"disambiguationData":[TD([[subQ2,1.0]])],"derivedFrom":subQ1}),-1.0]])]});}
            var Q71;
            {var subQ0=sQuery(id+"F6.wireOp",EDGE,"E12");var subQ1=makeQuery(id+"F6.imprint","INTERSECT",VERTEX,{"derivedFrom":[sQuery(id+"F6.wireOp",EDGE,"Tb1vFxD2-eZhD-3B21-jOu3-oEgeX6T2umbS"),subQ0]});Q71=makeQuery(id+"F6.imprint","IMPRINT",FACE,{"disambiguationData":[TD([[makeQuery(id+"F6.imprint","IMPRINT",EDGE,{"disambiguationData":[TD([[subQ1,1.0]])],"derivedFrom":subQ0}),1.0]])]});}
            extrude(context, id + "F7", {"entities" : qUnion([Q0, Q1, Q2, Q3, Q4, Q5, Q6, Q7, Q8, Q9, Q10, Q11, Q12, Q13, Q14, Q15, Q16, Q17, Q18, Q19, Q20, Q21, Q22, Q23, Q24, Q25, Q26, Q27, Q28, Q29, Q30, Q31, Q32, Q33, Q34, Q35, Q36, Q37, Q38, Q39, Q40, Q41, Q42, Q43, Q44, Q45, Q46, Q47, Q48, Q49, Q50, Q51, Q52, Q53, Q54, Q55, Q56, Q57, Q58, Q59, Q60, Q61, Q62, Q63, Q64, Q65, Q66, Q67, Q68, Q69, Q70, Q71]), "operationType" : NewBodyOperationType.REMOVE, "oppositeDirection" : true, "depth" : 142.34 * mm});
        }
    });
